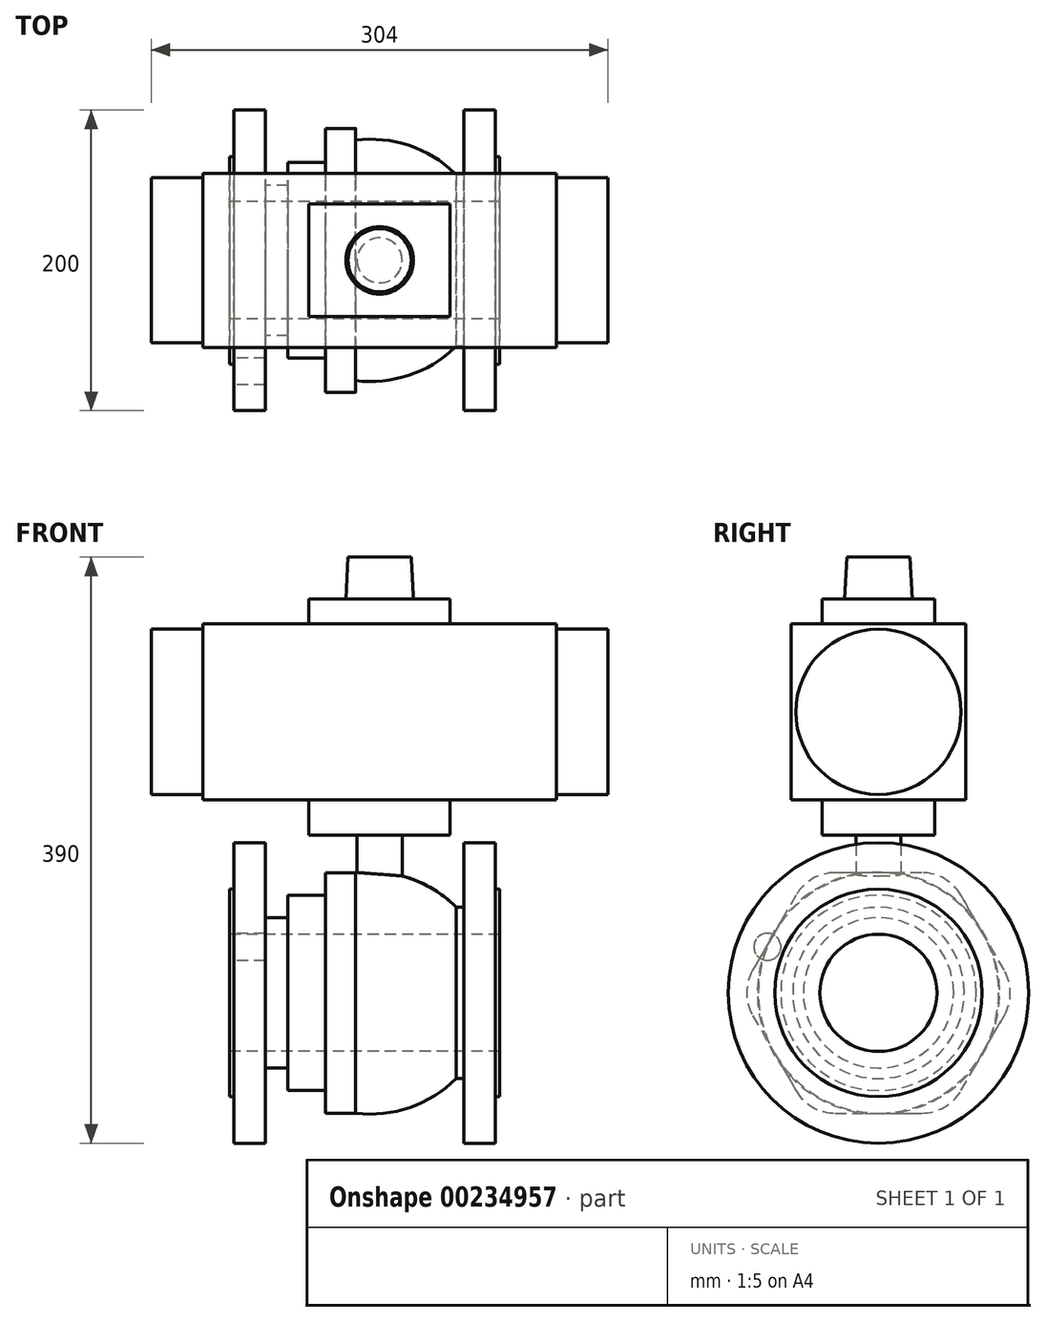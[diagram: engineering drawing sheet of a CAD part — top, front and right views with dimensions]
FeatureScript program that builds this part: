
annotation { "Feature Type Name" : "Feature", "Feature Type Description" : "" }
export const myFeature = defineFeature(function(context is Context, id is Id, definition is map)
    precondition{}
    {
        {
            var Q0;
            Q0=qCreatedBy(makeId("Front.planeOp"),FACE);
            var sketch = newSketch(context, id + "F0", { "sketchPlane" : qUnion([Q0])});
            skLineSegment(sketch, "E0", {"start": v(0, 0) * mm, "end": v(0, 69) * mm});
            skLineSegment(sketch, "E1", {"start": v(0, 69) * mm, "end": v(3, 69) * mm});
            skLineSegment(sketch, "E2", {"start": v(3, 69) * mm, "end": v(3, 100) * mm});
            skLineSegment(sketch, "E3", {"start": v(3, 100) * mm, "end": v(24, 100) * mm});
            skLineSegment(sketch, "E4", {"start": v(24, 100) * mm, "end": v(24, 50) * mm});
            skLineSegment(sketch, "E5", {"start": v(24, 50) * mm, "end": v(39, 50) * mm});
            skLineSegment(sketch, "E6", {"start": v(39, 50) * mm, "end": v(39, 65) * mm});
            skLineSegment(sketch, "E7", {"start": v(39, 65) * mm, "end": v(64, 65) * mm});
            skLineSegment(sketch, "E8", {"start": v(64, 65) * mm, "end": v(64, 90) * mm});
            skLineSegment(sketch, "E9", {"start": v(64, 90) * mm, "end": v(84, 90) * mm});
            skLineSegment(sketch, "E10.MirrorCS", {"start": v(156, 100) * mm, "end": v(156, 57) * mm});
            skLineSegment(sketch, "E11", {"start": v(156, 57) * mm, "end": v(151, 57) * mm});
            skLineSegment(sketch, "E12", {"start": v(0, 0) * mm, "end": v(180, 0) * mm});
            skLineSegment(sketch, "E13", {"start": v(156, 100) * mm, "end": v(177, 100) * mm});
            skLineSegment(sketch, "E14", {"start": v(177, 100) * mm, "end": v(177, 69) * mm});
            skLineSegment(sketch, "E15", {"start": v(177, 69) * mm, "end": v(180, 69) * mm});
            skLineSegment(sketch, "E16", {"start": v(180, 69) * mm, "end": v(180, 0) * mm});
            skLineSegment(sketch, "E17", {"start": v(84, 90) * mm, "end": v(84, 80) * mm});
            skArc(sketch, "E18", {"start": v(151, 57) * mm, "mid": v(120.16, 76.25) * mm, "end": v(84, 80) * mm});
            skSolve(sketch);
        }
        {
            var Q0;
            Q0=makeQuery(id+"F0.imprint","IMPRINT",FACE,{"disambiguationData":[TD([[makeQuery(id+"F0.imprint","IMPRINT",EDGE,{"derivedFrom":sQuery(id+"F0.wireOp",EDGE,"E0")}),-1.0]])]});
            var Q1;
            Q1=sQuery(id+"F0.wireOp",EDGE,"E12");
            revolve(context, id + "F1", {"entities" : qUnion([Q0]), "axis" : qUnion([Q1]), "revolveType" : RevolveType.FULL});
        }
        {
            var Q0;
            Q0=qCreatedBy(makeId("Top.planeOp"),FACE);
            var sketch = newSketch(context, id + "F2", { "sketchPlane" : qUnion([Q0])});
            skCircle(sketch, "E19", {"center": v(100, 0) * mm, "radius": 15 * mm});
            skLineSegment(sketch, "E20", {"start": v(100, -63.5) * mm, "end": v(100, 63.5) * mm, "construction": true});
            skLineSegment(sketch, "E21", {"start": v(-17.5, 0) * mm, "end": v(217.5, 0) * mm, "construction": true});
            skSolve(sketch);
        }
        {
            var Q0;
            Q0=makeQuery(id+"F2.imprint","IMPRINT",FACE,{"disambiguationData":[TD([[makeQuery(id+"F2.imprint","IMPRINT",EDGE,{"derivedFrom":sQuery(id+"F2.wireOp",EDGE,"E19")}),1.0]])]});
            extrude(context, id + "F3", {"entities" : qUnion([Q0]), "operationType" : NewBodyOperationType.ADD, "depth" : 105 * mm});
        }
        {
            var Q0;
            Q0=makeQuery(id+"F3.opExtrude","CAP_FACE",FACE,{"disambiguationData":[OSD([sQuery(id+"F2.wireOp",EDGE,"E19")])],"isStart":false});
            cPlane(context, id + "F4", {"entities" : qUnion([Q0]), "cplaneType" : CPlaneType.OFFSET, "offset" : 0 * mm, "width" : 150 * mm, "height" : 150 * mm});
        }
        {
            var Q0;
            Q0=qCreatedBy(id+"F4.planeOp",FACE);
            var sketch = newSketch(context, id + "F5", { "sketchPlane" : qUnion([Q0])});
            skLineSegment(sketch, "E22.bottom", {"start": v(53, 37.5) * mm, "end": v(147, 37.5) * mm});
            skLineSegment(sketch, "E22.top", {"start": v(53, -37.5) * mm, "end": v(147, -37.5) * mm});
            skLineSegment(sketch, "E22.left", {"start": v(53, 37.5) * mm, "end": v(53, -37.5) * mm});
            skLineSegment(sketch, "E22.right", {"start": v(147, 37.5) * mm, "end": v(147, -37.5) * mm});
            skPoint(sketch, "E23", {"position": v(100, 37.5) * mm});
            skPoint(sketch, "E24", {"position": v(147, 0) * mm});
            skSolve(sketch);
        }
        {
            var Q0;
            Q0 = qSketchRegion(id + "F5", true);
            extrude(context, id + "F6", {"entities" : qUnion([Q0]), "operationType" : NewBodyOperationType.ADD, "depth" : 157 * mm});
        }
        {
            var Q0;
            Q0=makeQuery(id+"F6.opExtrude","CAP_FACE",FACE,{"disambiguationData":[OSD([sQuery(id+"F5.wireOp",EDGE,"E22.bottom"),sQuery(id+"F5.wireOp",EDGE,"E22.top"),sQuery(id+"F5.wireOp",EDGE,"E22.left"),sQuery(id+"F5.wireOp",EDGE,"E22.right")])],"isStart":true});
            cPlane(context, id + "F7", {"entities" : qUnion([Q0]), "cplaneType" : CPlaneType.OFFSET, "offset" : 23.5 * mm, "oppositeDirection" : true, "width" : 150 * mm, "height" : 150 * mm});
        }
        {
            var Q0;
            Q0=qCreatedBy(id+"F7.planeOp",FACE);
            var sketch = newSketch(context, id + "F8", { "sketchPlane" : qUnion([Q0])});
            skLineSegment(sketch, "E25.bottom", {"start": v(-17.5, 58) * mm, "end": v(217.5, 58) * mm});
            skLineSegment(sketch, "E25.top", {"start": v(-17.5, -58) * mm, "end": v(217.5, -58) * mm});
            skLineSegment(sketch, "E25.left", {"start": v(-17.5, 58) * mm, "end": v(-17.5, -58) * mm});
            skLineSegment(sketch, "E25.right", {"start": v(217.5, 58) * mm, "end": v(217.5, -58) * mm});
            skPoint(sketch, "E26", {"position": v(100, 58) * mm});
            skPoint(sketch, "E27", {"position": v(217.5, 0) * mm});
            skSolve(sketch);
        }
        {
            var Q0;
            Q0=makeQuery(id+"F8.imprint","IMPRINT",FACE,{"disambiguationData":[TD([[makeQuery(id+"F8.imprint","IMPRINT",EDGE,{"derivedFrom":sQuery(id+"F8.wireOp",EDGE,"E25.bottom")}),-1.0]])]});
            extrude(context, id + "F9", {"entities" : qUnion([Q0]), "operationType" : NewBodyOperationType.ADD, "oppositeDirection" : true, "depth" : 117 * mm});
        }
        {
            var Q0;
            Q0=makeQuery(id+"F9.opExtrude","SWEPT_FACE",FACE,{"disambiguationData":[OSD([sQuery(id+"F8.wireOp",EDGE,"E25.right")])]});
            cPlane(context, id + "F10", {"entities" : qUnion([Q0]), "cplaneType" : CPlaneType.OFFSET, "offset" : 0 * mm, "width" : 150 * mm, "height" : 150 * mm});
        }
        {
            var Q0;
            Q0=qCreatedBy(id+"F10.planeOp",FACE);
            var sketch = newSketch(context, id + "F11", { "sketchPlane" : qUnion([Q0])});
            skCircle(sketch, "E28", {"center": v(0, 187) * mm, "radius": 55 * mm});
            skSolve(sketch);
        }
        {
            var Q0;
            Q0 = qSketchRegion(id + "F11", true);
            extrude(context, id + "F12", {"entities" : qUnion([Q0]), "operationType" : NewBodyOperationType.ADD, "depth" : 34.5 * mm, "hasSecondDirection" : true, "secondDirectionOppositeDirection" : true, "secondDirectionDepth" : 269.5 * mm});
        }
        {
            var Q0;
            Q0=makeQuery(id+"F6.opExtrude","CAP_FACE",FACE,{"disambiguationData":[OSD([sQuery(id+"F5.wireOp",EDGE,"E22.bottom"),sQuery(id+"F5.wireOp",EDGE,"E22.top"),sQuery(id+"F5.wireOp",EDGE,"E22.left"),sQuery(id+"F5.wireOp",EDGE,"E22.right")])],"isStart":false});
            cPlane(context, id + "F13", {"entities" : qUnion([Q0]), "cplaneType" : CPlaneType.OFFSET, "offset" : 0 * mm, "width" : 150 * mm, "height" : 150 * mm});
        }
        {
            var Q0;
            Q0=qCreatedBy(id+"F13.planeOp",FACE);
            var sketch = newSketch(context, id + "F14", { "sketchPlane" : qUnion([Q0])});
            skCircle(sketch, "E29", {"center": v(100, 0) * mm, "radius": 22.5 * mm});
            skSolve(sketch);
        }
        {
            var Q0;
            Q0 = qSketchRegion(id + "F14", true);
            extrude(context, id + "F15", {"entities" : qUnion([Q0]), "operationType" : NewBodyOperationType.ADD, "depth" : 28 * mm, "hasDraft" : true, "draftAngle" : 3 * degree, "draftPullDirection" : true});
        }
        {
            var Q0;
            Q0=qCreatedBy(makeId("Right.planeOp"),FACE);
            var sketch = newSketch(context, id + "F16", { "sketchPlane" : qUnion([Q0])});
            skCircle(sketch, "E30", {"center": v(0, 0) * mm, "radius": 39 * mm});
            skSolve(sketch);
        }
        {
            var Q0;
            Q0 = qSketchRegion(id + "F16", true);
            extrude(context, id + "F17", {"entities" : qUnion([Q0]), "operationType" : NewBodyOperationType.REMOVE, "endBound" : BoundingType.THROUGH_ALL, "depth" : 25 * mm});
        }
        {
            var Q0;
            Q0=makeQuery(id+"F1.opRevolve","SWEPT_FACE",FACE,{"disambiguationData":[OSD([sQuery(id+"F0.wireOp",EDGE,"E8")])]});
            cPlane(context, id + "F18", {"entities" : qUnion([Q0]), "cplaneType" : CPlaneType.OFFSET, "offset" : 0 * mm, "width" : 150 * mm, "height" : 150 * mm});
        }
        {
            var Q0;
            Q0=qCreatedBy(id+"F18.planeOp",FACE);
            var sketch = newSketch(context, id + "F19", { "sketchPlane" : qUnion([Q0])});
            skCircle(sketch, "E31.cCircle", {"center": v(0, 0) * mm, "radius": 80 * mm, "construction": true});
            skLineSegment(sketch, "E31.0", {"start": v(54.85, 65) * mm, "end": v(83.72, 15) * mm});
            skLineSegment(sketch, "E31.1", {"start": v(83.72, -15) * mm, "end": v(54.85, -65) * mm});
            skLineSegment(sketch, "E31.2", {"start": v(28.87, -80) * mm, "end": v(-28.87, -80) * mm});
            skLineSegment(sketch, "E31.3", {"start": v(-54.85, -65) * mm, "end": v(-83.72, -15) * mm});
            skLineSegment(sketch, "E31.4", {"start": v(-83.72, 15) * mm, "end": v(-54.85, 65) * mm});
            skLineSegment(sketch, "E31.5", {"start": v(-28.87, 80) * mm, "end": v(28.87, 80) * mm});
            skPoint(sketch, "E31.0.midPoint", {"position": v(69.28, 40) * mm});
            skPoint(sketch, "E32.orphan", {"position": v(-46.19, 80) * mm});
            skPoint(sketch, "E33.orphan", {"position": v(-92.38, 0) * mm});
            skPoint(sketch, "E34.orphan", {"position": v(-46.19, -80) * mm});
            skPoint(sketch, "E35.orphan", {"position": v(46.19, -80) * mm});
            skPoint(sketch, "E36.orphan", {"position": v(92.38, 0) * mm});
            skPoint(sketch, "E37.orphan", {"position": v(46.19, 80) * mm});
            skArc(sketch, "E38.filletArc", {"start": v(54.85, 65) * mm, "mid": v(43.87, 75.98) * mm, "end": v(28.87, 80) * mm});
            skArc(sketch, "E39.filletArc", {"start": v(-28.87, 80) * mm, "mid": v(-43.87, 75.98) * mm, "end": v(-54.85, 65) * mm});
            skArc(sketch, "E40.filletArc", {"start": v(-83.72, 15) * mm, "mid": v(-87.74, 0) * mm, "end": v(-83.72, -15) * mm});
            skArc(sketch, "E41.filletArc", {"start": v(-54.85, -65) * mm, "mid": v(-43.87, -75.98) * mm, "end": v(-28.87, -80) * mm});
            skArc(sketch, "E42.filletArc", {"start": v(28.87, -80) * mm, "mid": v(43.87, -75.98) * mm, "end": v(54.85, -65) * mm});
            skArc(sketch, "E43.filletArc", {"start": v(83.72, -15) * mm, "mid": v(87.74, 0) * mm, "end": v(83.72, 15) * mm});
            skCircle(sketch, "E44", {"center": v(0, 0) * mm, "radius": 90 * mm});
            skSolve(sketch);
        }
        {
            var Q0;
            Q0 = qSketchRegion(id + "F19", true);
            var Q1;
            Q1=makeQuery(id+"F1.opRevolve","SWEPT_FACE",FACE,{"disambiguationData":[OSD([sQuery(id+"F0.wireOp",EDGE,"E17")])]});
            extrude(context, id + "F20", {"entities" : qUnion([Q0]), "operationType" : NewBodyOperationType.REMOVE, "endBound" : BoundingType.UP_TO_SURFACE, "oppositeDirection" : true, "endBoundEntityFace" : qUnion([Q1]), "depth" : 25 * mm});
        }
        {
            var Q0;
            Q0=qCreatedBy(makeId("Right.planeOp"),FACE);
            var sketch = newSketch(context, id + "F21", { "sketchPlane" : qUnion([Q0])});
            skCircle(sketch, "E45", {"center": v(-73.91, 30.61) * mm, "radius": 9 * mm});
            skLineSegment(sketch, "E46", {"start": v(-73.91, 30.61) * mm, "end": v(0, 0) * mm, "construction": true});
            skSolve(sketch);
        }
        {
            var Q0;
            Q0 = qSketchRegion(id + "F21", true);
            var Q1;
            Q1=makeQuery(id+"F1.opRevolve","SWEPT_FACE",FACE,{"disambiguationData":[OSD([sQuery(id+"F0.wireOp",EDGE,"E4")])]});
            extrude(context, id + "F22", {"entities" : qUnion([Q0]), "operationType" : NewBodyOperationType.REMOVE, "endBoundEntityFace" : qUnion([Q1]), "depth" : 24 * mm});
        }
        {
            var Q0;
            Q0=qCreatedBy(makeId("Right.planeOp"),FACE);
            cPlane(context, id + "F23", {"entities" : qUnion([Q0]), "cplaneType" : CPlaneType.OFFSET, "offset" : 90 * mm, "width" : 150 * mm, "height" : 150 * mm});
        }
    });
